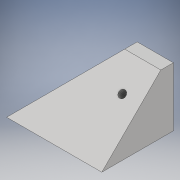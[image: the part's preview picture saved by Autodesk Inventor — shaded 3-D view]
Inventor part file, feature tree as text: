
AUTODESK INVENTOR PART (.ipt)
format: ipt  version: 2019 (Build 230136000, 136)  size: 135,168 bytes
history: native  units: mm
features: sketch x5, hole x3, extrude x2, other x1
ambient origin geometry x8: Origin, YZ Plane, XZ Plane, XY Plane, X Axis, Y Axis, Z Axis, Center Point
bodies: Body1 (feature_tree)
feature tree (11):
  other  "Bryła1"
  extrude  "Wyciągnięcie proste1"  Depth=20.0mm
  extrude  "Wyciągnięcie proste2"  Depth=24.25mm
  hole  "Otwór1"  [1 undecoded]
  hole  "Otwór2"  [1 undecoded]
  hole  "Otwór3"  [1 undecoded]
  sketch  "Szkic1"
  sketch  "Szkic2"
  sketch  "Szkic3"
  sketch  "Szkic4"
  sketch  "Szkic5"
note: 3 required parameter values undecoded (feature->parameter linkage not recoverable at this tier; creation-order binding heuristic only, values carry confidence <= 0.55)
